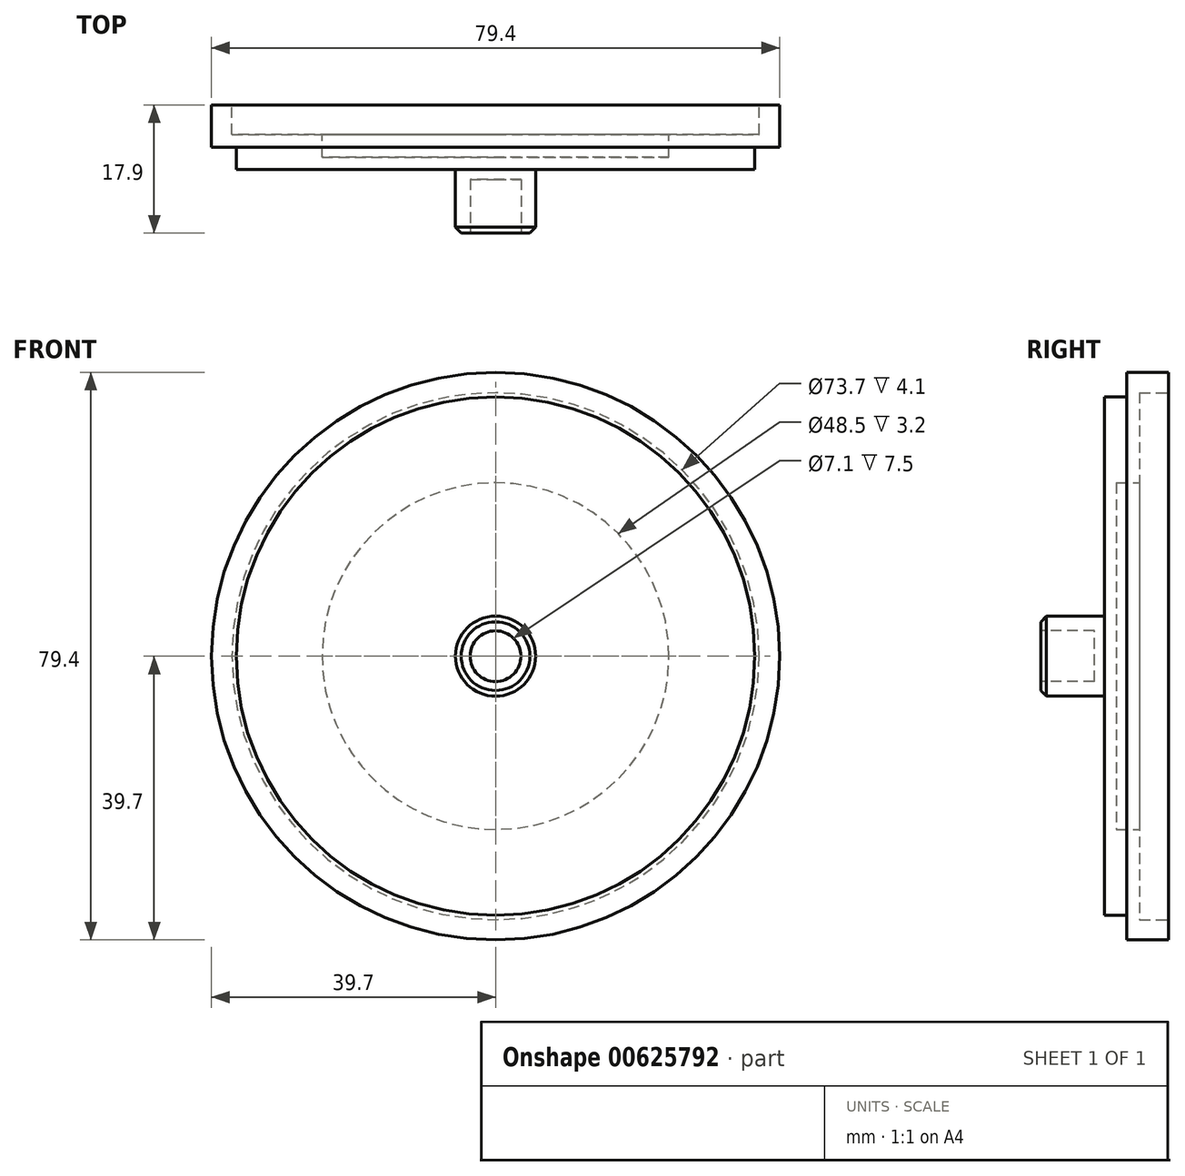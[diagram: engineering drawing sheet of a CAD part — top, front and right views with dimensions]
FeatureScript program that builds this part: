
annotation { "Feature Type Name" : "Feature", "Feature Type Description" : "" }
export const myFeature = defineFeature(function(context is Context, id is Id, definition is map)
    precondition{}
    {
        {
            var Q0;
            Q0=qCreatedBy(makeId("Front.planeOp"),FACE);
            var sketch = newSketch(context, id + "F0", { "sketchPlane" : qUnion([Q0])});
            skCircle(sketch, "E0", {"center": v(0, 0) * mm, "radius": 39.7 * mm});
            skSolve(sketch);
        }
        {
            var Q0;
            Q0 = qSketchRegion(id + "F0", true);
            extrude(context, id + "F1", {"entities" : qUnion([Q0]), "depth" : 5.9 * mm, "offsetDistance" : 25 * mm});
        }
        {
            var Q0;
            Q0=makeQuery(id+"F1.opExtrude","CAP_FACE",FACE,{"disambiguationData":[OSD([sQuery(id+"F0.wireOp",EDGE,"E0")])],"isStart":false});
            var sketch = newSketch(context, id + "F2", { "sketchPlane" : qUnion([Q0])});
            skCircle(sketch, "E1", {"center": v(0, 0) * mm, "radius": 36.25 * mm});
            skSolve(sketch);
        }
        {
            var Q0;
            Q0 = qSketchRegion(id + "F2", true);
            extrude(context, id + "F3", {"entities" : qUnion([Q0]), "operationType" : NewBodyOperationType.ADD, "depth" : 3.1 * mm, "offsetDistance" : 25 * mm});
        }
        {
            var Q0;
            Q0=makeQuery(id+"F3.opExtrude","CAP_FACE",FACE,{"disambiguationData":[OSD([sQuery(id+"F2.wireOp",EDGE,"E1")])],"isStart":false});
            var sketch = newSketch(context, id + "F4", { "sketchPlane" : qUnion([Q0])});
            skCircle(sketch, "E2", {"center": v(0, 0) * mm, "radius": 5.6 * mm});
            skSolve(sketch);
        }
        {
            var Q0;
            Q0 = qSketchRegion(id + "F4", true);
            extrude(context, id + "F5", {"entities" : qUnion([Q0]), "operationType" : NewBodyOperationType.ADD, "depth" : 8.9 * mm, "offsetDistance" : 25 * mm});
        }
        {
            var Q0;
            Q0=makeQuery(id+"F1.opExtrude","CAP_FACE",FACE,{"disambiguationData":[OSD([sQuery(id+"F0.wireOp",EDGE,"E0")])],"isStart":true});
            var sketch = newSketch(context, id + "F6", { "sketchPlane" : qUnion([Q0])});
            skCircle(sketch, "E3", {"center": v(0, 0) * mm, "radius": 36.85 * mm});
            skSolve(sketch);
        }
        {
            var Q0;
            Q0 = qSketchRegion(id + "F6", true);
            extrude(context, id + "F7", {"entities" : qUnion([Q0]), "operationType" : NewBodyOperationType.REMOVE, "oppositeDirection" : true, "depth" : 4.1 * mm, "offsetDistance" : 25 * mm});
        }
        {
            var Q0;
            Q0=makeQuery(id+"F7.boolean.opBoolean","COPY",FACE,{"derivedFrom":makeQuery(id+"F7.opExtrude","CAP_FACE",FACE,{"disambiguationData":[OSD([sQuery(id+"F6.wireOp",EDGE,"E3")])],"isStart":false})});
            var sketch = newSketch(context, id + "F8", { "sketchPlane" : qUnion([Q0])});
            skCircle(sketch, "E4", {"center": v(0, 0) * mm, "radius": 24.25 * mm});
            skSolve(sketch);
        }
        {
            var Q0;
            Q0 = qSketchRegion(id + "F8", true);
            extrude(context, id + "F9", {"entities" : qUnion([Q0]), "operationType" : NewBodyOperationType.REMOVE, "oppositeDirection" : true, "depth" : 3.2 * mm, "offsetDistance" : 25 * mm});
        }
        {
            var Q0;
            Q0=makeQuery(id+"F5.opExtrude","CAP_FACE",FACE,{"disambiguationData":[OSD([sQuery(id+"F4.wireOp",EDGE,"E2")])],"isStart":false});
            var sketch = newSketch(context, id + "F10", { "sketchPlane" : qUnion([Q0])});
            skCircle(sketch, "E5", {"center": v(0, 0) * mm, "radius": 3.55 * mm});
            skSolve(sketch);
        }
        {
            var Q0;
            Q0 = qSketchRegion(id + "F10", true);
            extrude(context, id + "F11", {"entities" : qUnion([Q0]), "operationType" : NewBodyOperationType.REMOVE, "oppositeDirection" : true, "depth" : 7.5 * mm, "offsetDistance" : 25 * mm});
        }
        {
            var Q0;
            Q0=makeQuery(id+"F5.opExtrude","CAP_EDGE",EDGE,{"disambiguationData":[OSD([sQuery(id+"F4.wireOp",EDGE,"E2")])],"isStart":false});
            chamfer(context, id + "F12", {"entities" : qUnion([Q0]), "width" : 0.8 * mm, "tangentPropagation" : true});
        }
    });
